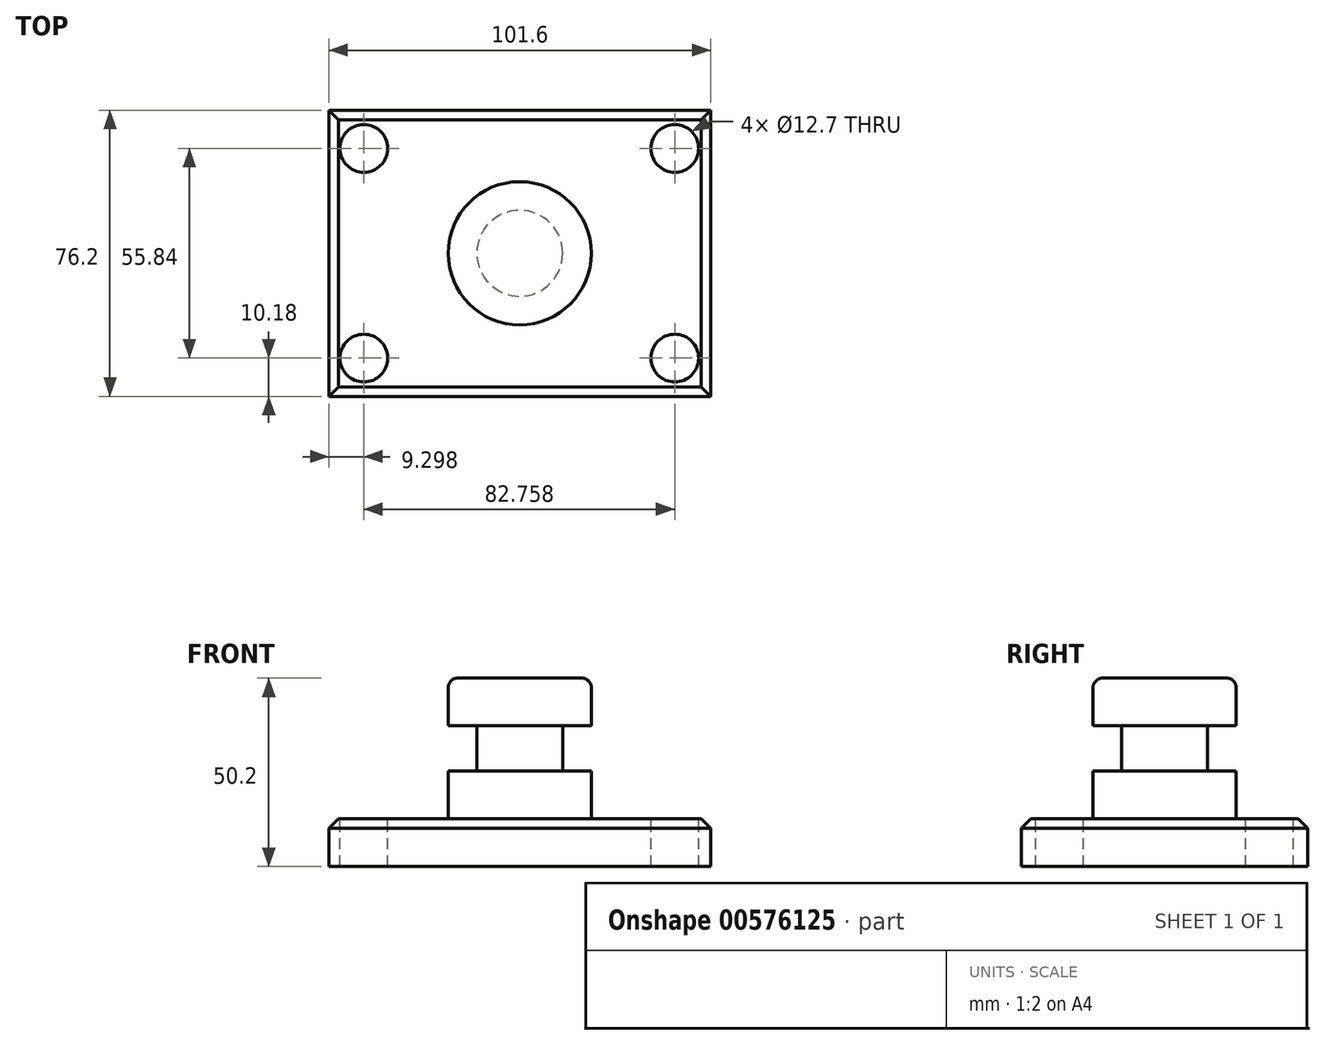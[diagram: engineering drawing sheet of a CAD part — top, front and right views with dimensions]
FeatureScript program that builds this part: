
annotation { "Feature Type Name" : "Feature", "Feature Type Description" : "" }
export const myFeature = defineFeature(function(context is Context, id is Id, definition is map)
    precondition{}
    {
        {
            var Q0;
            Q0=qCreatedBy(makeId("Top.planeOp"),FACE);
            var sketch = newSketch(context, id + "F0", { "sketchPlane" : qUnion([Q0])});
            skLineSegment(sketch, "E0.bottom", {"start": v(50.8, -38.1) * mm, "end": v(-50.8, -38.1) * mm});
            skLineSegment(sketch, "E0.top", {"start": v(50.8, 38.1) * mm, "end": v(-50.8, 38.1) * mm});
            skLineSegment(sketch, "E0.left", {"start": v(50.8, -38.1) * mm, "end": v(50.8, 38.1) * mm});
            skLineSegment(sketch, "E0.right", {"start": v(-50.8, -38.1) * mm, "end": v(-50.8, 38.1) * mm});
            skPoint(sketch, "E0.middle", {"position": v(0, 0) * mm});
            skSolve(sketch);
        }
        {
            var Q0;
            Q0=makeQuery(id+"F0.imprint","IMPRINT",FACE,{"disambiguationData":[TD([[makeQuery(id+"F0.imprint","IMPRINT",EDGE,{"derivedFrom":sQuery(id+"F0.wireOp",EDGE,"E0.bottom")}),-1.0]])]});
            extrude(context, id + "F1", {"entities" : qUnion([Q0]), "depth" : 12.7 * mm, "offsetDistance" : 25.4 * mm});
        }
        {
            var Q0;
            Q0=makeQuery(id+"F1.opExtrude","CAP_FACE",FACE,{"disambiguationData":[OSD([sQuery(id+"F0.wireOp",EDGE,"E0.bottom"),sQuery(id+"F0.wireOp",EDGE,"E0.top"),sQuery(id+"F0.wireOp",EDGE,"E0.left"),sQuery(id+"F0.wireOp",EDGE,"E0.right")])],"isStart":false});
            var sketch = newSketch(context, id + "F2", { "sketchPlane" : qUnion([Q0])});
            skSolve(sketch);
        }
        {
            var Q0;
            Q0=makeQuery(id+"F2.imprint","IMPRINT",FACE,{"disambiguationData":[TD([[makeQuery(id+"F2.imprint","IMPRINT",EDGE,{"derivedFrom":makeQuery(id+"F1.opExtrude","CAP_EDGE",EDGE,{"disambiguationData":[OSD([sQuery(id+"F0.wireOp",EDGE,"E0.bottom")])],"isStart":false})}),-1.0]])]});
            var sketch = newSketch(context, id + "F3", { "sketchPlane" : qUnion([Q0])});
            skPoint(sketch, "E1.middle", {"position": v(-0.12, 0) * mm});
            skLineSegment(sketch, "E2.bottom", {"start": v(41.26, 27.92) * mm, "end": v(-41.5, 27.92) * mm});
            skLineSegment(sketch, "E2.top", {"start": v(41.26, -27.92) * mm, "end": v(-41.5, -27.92) * mm});
            skLineSegment(sketch, "E2.left", {"start": v(41.26, 27.92) * mm, "end": v(41.26, -27.92) * mm});
            skLineSegment(sketch, "E2.right", {"start": v(-41.5, 27.92) * mm, "end": v(-41.5, -27.92) * mm});
            skSolve(sketch);
        }
        {
            var Q0;
            Q0=sQuery(id+"F3.wireOp",VERTEX,"E2.right.start");
            var Q1;
            Q1=sQuery(id+"F3.wireOp",VERTEX,"E2.left.start");
            var Q2;
            Q2=sQuery(id+"F3.wireOp",VERTEX,"E2.left.end");
            var Q3;
            Q3=sQuery(id+"F3.wireOp",VERTEX,"E2.top.end");
            var Q4;
            Q4=makeQuery(id+"F1.opExtrude","SWEPT_BODY",BODY,{"disambiguationData":[OSD([sQuery(id+"F0.wireOp",EDGE,"E0.bottom"),sQuery(id+"F0.wireOp",EDGE,"E0.top"),sQuery(id+"F0.wireOp",EDGE,"E0.left"),sQuery(id+"F0.wireOp",EDGE,"E0.right")])]});
            hole(context, id + "F4", {"style" : HoleStyle.SIMPLE, "endStyle" : HoleEndStyle.THROUGH, "holeDiameter" : 12.7 * mm, "isTappedThrough" : true, "tappedDepth" : 12.7 * mm, "tapClearance" : 3, "locations" : qUnion([Q0, Q1, Q2, Q3]), "scope" : qUnion([Q4])});
        }
        {
            var Q0;
            Q0=qCreatedBy(makeId("Front.planeOp"),FACE);
            var sketch = newSketch(context, id + "F5", { "sketchPlane" : qUnion([Q0])});
            skLineSegment(sketch, "E3.bottom", {"start": v(0, 12.7) * mm, "end": v(11.43, 12.7) * mm});
            skLineSegment(sketch, "E3.top", {"start": v(0, 44.45) * mm, "end": v(11.43, 44.45) * mm});
            skLineSegment(sketch, "E3.left", {"start": v(0, 12.7) * mm, "end": v(0, 44.45) * mm});
            skLineSegment(sketch, "E3.right", {"start": v(11.43, 12.7) * mm, "end": v(11.43, 44.45) * mm});
            skSolve(sketch);
        }
        {
            var Q0;
            Q0=makeQuery(id+"F5.imprint","IMPRINT",FACE,{"disambiguationData":[TD([[makeQuery(id+"F5.imprint","IMPRINT",EDGE,{"derivedFrom":sQuery(id+"F5.wireOp",EDGE,"E3.bottom")}),1.0]])]});
            var Q1;
            Q1=sQuery(id+"F5.wireOp",EDGE,"E3.left");
            revolve(context, id + "F6", {"operationType" : NewBodyOperationType.ADD, "entities" : qUnion([Q0]), "axis" : qUnion([Q1]), "revolveType" : RevolveType.FULL});
        }
        {
            var Q0;
            Q0=qCreatedBy(makeId("Front.planeOp"),FACE);
            var sketch = newSketch(context, id + "F7", { "sketchPlane" : qUnion([Q0])});
            skLineSegment(sketch, "E4.bottom", {"start": v(0, 12.7) * mm, "end": v(19.05, 12.7) * mm});
            skLineSegment(sketch, "E4.top", {"start": v(0, 25.4) * mm, "end": v(19.05, 25.4) * mm});
            skLineSegment(sketch, "E4.left", {"start": v(0, 12.7) * mm, "end": v(0, 25.4) * mm});
            skLineSegment(sketch, "E4.right", {"start": v(19.05, 12.7) * mm, "end": v(19.05, 25.4) * mm});
            skSolve(sketch);
        }
        {
            var Q0;
            Q0=makeQuery(id+"F7.imprint","IMPRINT",FACE,{"disambiguationData":[TD([[makeQuery(id+"F7.imprint","IMPRINT",EDGE,{"derivedFrom":sQuery(id+"F7.wireOp",EDGE,"E4.bottom")}),1.0]])]});
            var Q1;
            Q1=sQuery(id+"F7.wireOp",EDGE,"E4.left");
            revolve(context, id + "F8", {"operationType" : NewBodyOperationType.ADD, "entities" : qUnion([Q0]), "axis" : qUnion([Q1]), "revolveType" : RevolveType.FULL});
        }
        {
            var Q0;
            Q0=qCreatedBy(makeId("Front.planeOp"),FACE);
            var sketch = newSketch(context, id + "F9", { "sketchPlane" : qUnion([Q0])});
            skLineSegment(sketch, "E5.bottom", {"start": v(0, 37.5) * mm, "end": v(19.05, 37.5) * mm});
            skLineSegment(sketch, "E5.top", {"start": v(0, 50.2) * mm, "end": v(19.05, 50.2) * mm});
            skLineSegment(sketch, "E5.left", {"start": v(0, 37.5) * mm, "end": v(0, 50.2) * mm});
            skLineSegment(sketch, "E5.right", {"start": v(19.05, 37.5) * mm, "end": v(19.05, 50.2) * mm});
            skSolve(sketch);
        }
        {
            var Q0;
            Q0=makeQuery(id+"F9.imprint","IMPRINT",FACE,{"disambiguationData":[TD([[makeQuery(id+"F9.imprint","IMPRINT",EDGE,{"derivedFrom":sQuery(id+"F9.wireOp",EDGE,"E5.bottom")}),1.0]])]});
            var Q1;
            Q1=sQuery(id+"F9.wireOp",EDGE,"E5.left");
            revolve(context, id + "F10", {"operationType" : NewBodyOperationType.ADD, "entities" : qUnion([Q0]), "axis" : qUnion([Q1]), "revolveType" : RevolveType.FULL});
        }
        {
            var Q0;
            Q0=makeQuery(id+"F10.opRevolve","SWEPT_EDGE",EDGE,{"disambiguationData":[OSD([sQuery(id+"F9.wireOp",EDGE,"E5.top"),sQuery(id+"F9.wireOp",EDGE,"E5.right")])]});
            var Q1;
            Q1=makeQuery(id+"F8.opRevolve","SWEPT_EDGE",EDGE,{"disambiguationData":[OSD([sQuery(id+"F7.wireOp",EDGE,"E4.bottom"),sQuery(id+"F7.wireOp",EDGE,"E4.right")])]});
            fillet(context, id + "F11", {"entities" : qUnion([Q0, Q1]), "radius" : 2.54 * mm, "tangentPropagation" : true, "allowEdgeOverflow" : false});
        }
        {
            var Q0;
            Q0=makeQuery(id+"F1.opExtrude","CAP_EDGE",EDGE,{"disambiguationData":[OSD([sQuery(id+"F0.wireOp",EDGE,"E0.top")])],"isStart":false});
            var Q1;
            Q1=makeQuery(id+"F1.opExtrude","CAP_EDGE",EDGE,{"disambiguationData":[OSD([sQuery(id+"F0.wireOp",EDGE,"E0.left")])],"isStart":false});
            var Q2;
            Q2=makeQuery(id+"F1.opExtrude","CAP_EDGE",EDGE,{"disambiguationData":[OSD([sQuery(id+"F0.wireOp",EDGE,"E0.bottom")])],"isStart":false});
            var Q3;
            Q3=makeQuery(id+"F1.opExtrude","CAP_EDGE",EDGE,{"disambiguationData":[OSD([sQuery(id+"F0.wireOp",EDGE,"E0.right")])],"isStart":false});
            chamfer(context, id + "F12", {"entities" : qUnion([Q0, Q1, Q2, Q3]), "width" : 2.54 * mm, "tangentPropagation" : true});
        }
    });
